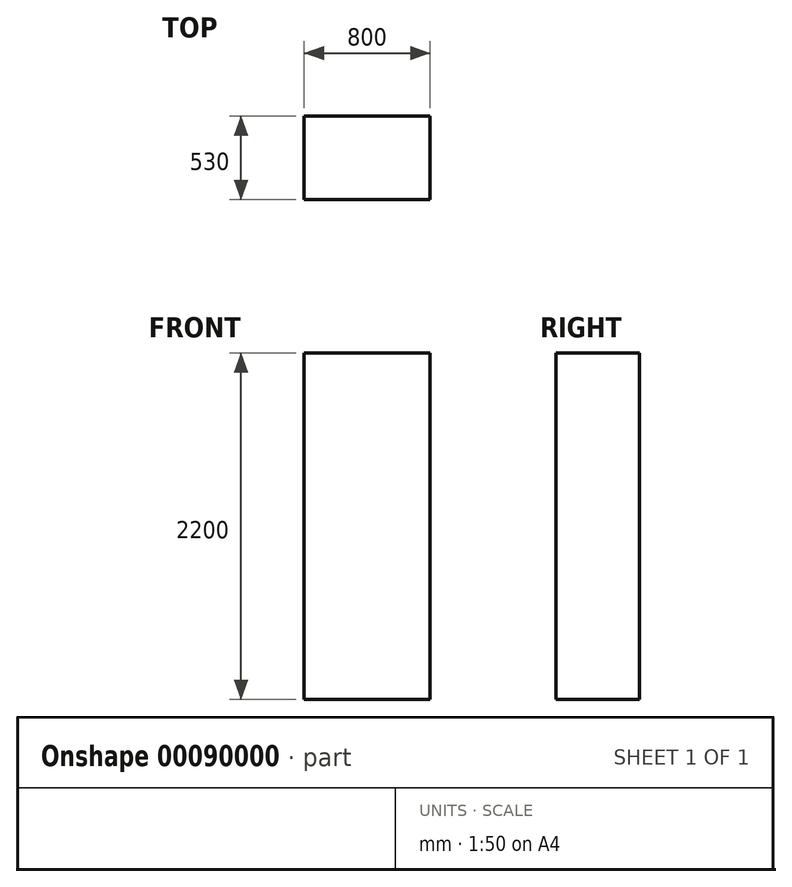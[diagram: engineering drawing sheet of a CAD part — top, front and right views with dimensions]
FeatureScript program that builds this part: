
annotation { "Feature Type Name" : "Feature", "Feature Type Description" : "" }
export const myFeature = defineFeature(function(context is Context, id is Id, definition is map)
    precondition{}
    {
        {
            var Q0;
            Q0=qCreatedBy(makeId("Top.planeOp"),FACE);
            var sketch = newSketch(context, id + "F0", { "sketchPlane" : qUnion([Q0])});
            skLineSegment(sketch, "E0.bottom", {"start": v(0, 0) * mm, "end": v(800, 0) * mm});
            skLineSegment(sketch, "E0.top", {"start": v(0, 530) * mm, "end": v(800, 530) * mm});
            skLineSegment(sketch, "E0.left", {"start": v(0, 0) * mm, "end": v(0, 530) * mm});
            skLineSegment(sketch, "E0.right", {"start": v(800, 0) * mm, "end": v(800, 530) * mm});
            skSolve(sketch);
        }
        {
            var Q0;
            Q0 = qSketchRegion(id + "F0", true);
            extrude(context, id + "F1", {"entities" : qUnion([Q0]), "depth" : 2200 * mm});
        }
    });
